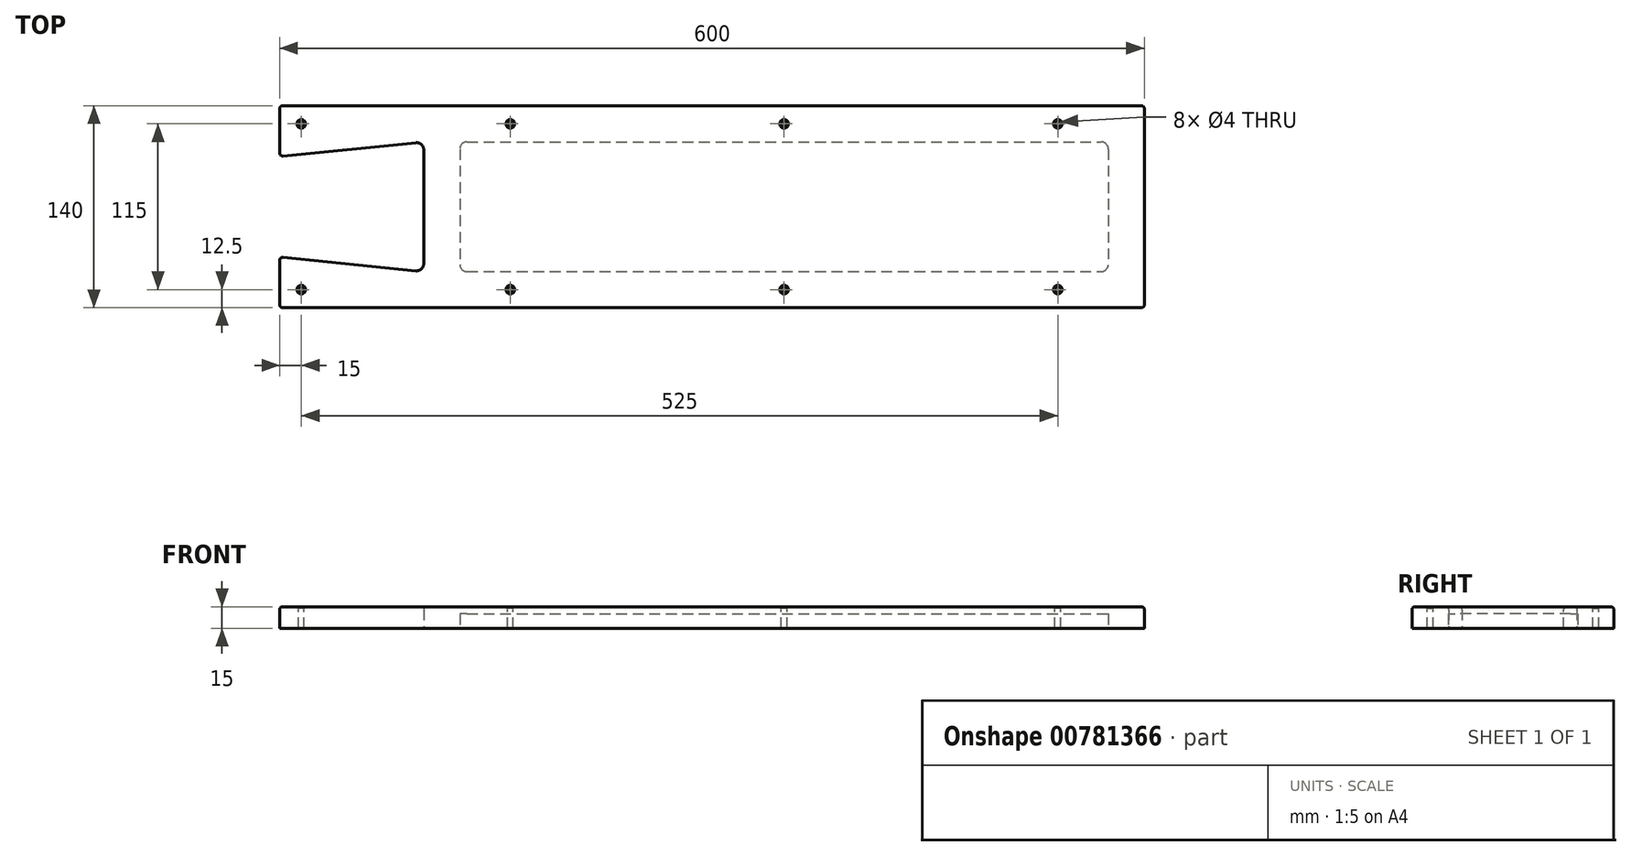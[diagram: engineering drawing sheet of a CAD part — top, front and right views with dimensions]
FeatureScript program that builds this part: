
annotation { "Feature Type Name" : "Feature", "Feature Type Description" : "" }
export const myFeature = defineFeature(function(context is Context, id is Id, definition is map)
    precondition{}
    {
        {
            var Q0;
            Q0=qCreatedBy(makeId("Top.planeOp"),FACE);
            var sketch = newSketch(context, id + "F0", { "sketchPlane" : qUnion([Q0])});
            skLineSegment(sketch, "E0.bottom", {"start": v(300, -70) * mm, "end": v(-300, -70) * mm});
            skLineSegment(sketch, "E0.top", {"start": v(300, 70) * mm, "end": v(-300, 70) * mm});
            skLineSegment(sketch, "E0.left", {"start": v(300, -70) * mm, "end": v(300, 70) * mm});
            skLineSegment(sketch, "E0.right", {"start": v(-300, -70) * mm, "end": v(-300, -35) * mm});
            skPoint(sketch, "E0.middle", {"position": v(0, 0) * mm});
            skLineSegment(sketch, "E1", {"start": v(0, 0) * mm, "end": v(-300, 0) * mm, "construction": true});
            skLineSegment(sketch, "E2", {"start": v(-300, 35) * mm, "end": v(-205.5, 44.45) * mm});
            skLineSegment(sketch, "E3", {"start": v(-200, 39.48) * mm, "end": v(-200, 0) * mm});
            skPoint(sketch, "E4.visualSharp", {"position": v(-200, 45) * mm});
            skArc(sketch, "E4.filletArc", {"start": v(-200, 39.48) * mm, "mid": v(-201.64, 43.18) * mm, "end": v(-205.5, 44.45) * mm});
            skLineSegment(sketch, "E5.MirrorCS", {"start": v(-300, -35) * mm, "end": v(-205.5, -44.45) * mm});
            skArc(sketch, "E6.MirrorCS", {"start": v(-200, -39.48) * mm, "mid": v(-201.64, -43.18) * mm, "end": v(-205.5, -44.45) * mm});
            skLineSegment(sketch, "E7.MirrorCS", {"start": v(-200, -39.48) * mm, "end": v(-200, 0) * mm});
            skLineSegment(sketch, "E8", {"start": v(-300, -35) * mm, "end": v(-300, 35) * mm, "construction": true});
            skLineSegment(sketch, "E9", {"start": v(-300, 35) * mm, "end": v(-300, 70) * mm});
            skSolve(sketch);
        }
        {
            var Q0;
            Q0=makeQuery(id+"F0.imprint","IMPRINT",FACE,{"disambiguationData":[TD([[makeQuery(id+"F0.imprint","IMPRINT",EDGE,{"derivedFrom":sQuery(id+"F0.wireOp",EDGE,"E0.bottom")}),-1.0]])]});
            extrude(context, id + "F1", {"entities" : qUnion([Q0]), "endBound" : BoundingType.SYMMETRIC, "depth" : 15 * mm, "offsetDistance" : 25 * mm});
        }
        {
            var Q0;
            Q0=makeQuery(id+"F1.opExtrude","CAP_FACE",FACE,{"disambiguationData":[OSD([sQuery(id+"F0.wireOp",EDGE,"E0.bottom"),sQuery(id+"F0.wireOp",EDGE,"E0.top"),sQuery(id+"F0.wireOp",EDGE,"E0.left"),sQuery(id+"F0.wireOp",EDGE,"E0.right"),sQuery(id+"F0.wireOp",EDGE,"E2"),sQuery(id+"F0.wireOp",EDGE,"E3"),sQuery(id+"F0.wireOp",EDGE,"E4.filletArc"),sQuery(id+"F0.wireOp",EDGE,"E5.MirrorCS"),sQuery(id+"F0.wireOp",EDGE,"E6.MirrorCS"),sQuery(id+"F0.wireOp",EDGE,"E7.MirrorCS"),sQuery(id+"F0.wireOp",EDGE,"E9")])],"isStart":true});
            var sketch = newSketch(context, id + "F2", { "sketchPlane" : qUnion([Q0])});
            skLineSegment(sketch, "E10", {"start": v(300, 0) * mm, "end": v(-200, 0) * mm, "construction": true});
            skLineSegment(sketch, "E11", {"start": v(-175, 0) * mm, "end": v(-175, 40) * mm});
            skLineSegment(sketch, "E12", {"start": v(-170, 45) * mm, "end": v(270, 45) * mm});
            skLineSegment(sketch, "E13", {"start": v(275, 40) * mm, "end": v(275, 0) * mm});
            skPoint(sketch, "E14.visualSharp", {"position": v(-175, 45) * mm});
            skArc(sketch, "E14.filletArc", {"start": v(-170, 45) * mm, "mid": v(-173.54, 43.54) * mm, "end": v(-175, 40) * mm});
            skPoint(sketch, "E15.visualSharp", {"position": v(275, 45) * mm});
            skArc(sketch, "E15.filletArc", {"start": v(275, 40) * mm, "mid": v(273.54, 43.54) * mm, "end": v(270, 45) * mm});
            skLineSegment(sketch, "E16.MirrorCS", {"start": v(-175, 0) * mm, "end": v(-175, -40) * mm});
            skArc(sketch, "E17.MirrorCS", {"start": v(-170, -45) * mm, "mid": v(-173.54, -43.54) * mm, "end": v(-175, -40) * mm});
            skLineSegment(sketch, "E18.MirrorCS", {"start": v(-170, -45) * mm, "end": v(270, -45) * mm});
            skArc(sketch, "E19.MirrorCS", {"start": v(275, -40) * mm, "mid": v(273.54, -43.54) * mm, "end": v(270, -45) * mm});
            skLineSegment(sketch, "E20.MirrorCS", {"start": v(275, -40) * mm, "end": v(275, 0) * mm});
            skSolve(sketch);
        }
        {
            var Q0;
            Q0=makeQuery(id+"F2.imprint","IMPRINT",FACE,{"disambiguationData":[TD([[makeQuery(id+"F2.imprint","IMPRINT",EDGE,{"derivedFrom":sQuery(id+"F2.wireOp",EDGE,"E11")}),-1.0]])]});
            extrude(context, id + "F3", {"entities" : qUnion([Q0]), "operationType" : NewBodyOperationType.REMOVE, "oppositeDirection" : true, "depth" : 10 * mm, "offsetDistance" : 25 * mm});
        }
        {
            var Q0;
            Q0=makeQuery(id+"F1.opExtrude","CAP_FACE",FACE,{"disambiguationData":[OSD([sQuery(id+"F0.wireOp",EDGE,"E0.bottom"),sQuery(id+"F0.wireOp",EDGE,"E0.top"),sQuery(id+"F0.wireOp",EDGE,"E0.left"),sQuery(id+"F0.wireOp",EDGE,"E0.right"),sQuery(id+"F0.wireOp",EDGE,"E2"),sQuery(id+"F0.wireOp",EDGE,"E3"),sQuery(id+"F0.wireOp",EDGE,"E4.filletArc"),sQuery(id+"F0.wireOp",EDGE,"E5.MirrorCS"),sQuery(id+"F0.wireOp",EDGE,"E6.MirrorCS"),sQuery(id+"F0.wireOp",EDGE,"E7.MirrorCS"),sQuery(id+"F0.wireOp",EDGE,"E9")])],"isStart":false});
            var sketch = newSketch(context, id + "F4", { "sketchPlane" : qUnion([Q0])});
            skLineSegment(sketch, "E21", {"start": v(-300, 57.5) * mm, "end": v(300, 57.5) * mm});
            skPoint(sketch, "E22", {"position": v(-285, 57.5) * mm});
            skLineSegment(sketch, "E23", {"start": v(0, 0) * mm, "end": v(-200, 0) * mm, "construction": true});
            skLineSegment(sketch, "E24.MirrorCS", {"start": v(-300, -57.5) * mm, "end": v(300, -57.5) * mm});
            skPoint(sketch, "E25.MirrorP", {"position": v(-285, -57.5) * mm});
            skPoint(sketch, "E26", {"position": v(-140, 57.5) * mm});
            skPoint(sketch, "E27", {"position": v(-140, -57.5) * mm});
            skPoint(sketch, "E28", {"position": v(50, 57.5) * mm});
            skPoint(sketch, "E29", {"position": v(50, -57.5) * mm});
            skPoint(sketch, "E30", {"position": v(240, 57.5) * mm});
            skPoint(sketch, "E31", {"position": v(240, -57.5) * mm});
            skSolve(sketch);
        }
        {
            var Q0;
            Q0=sQuery(id+"F4.wireOp",VERTEX,"E22");
            var Q1;
            Q1=sQuery(id+"F4.wireOp",VERTEX,"E25.MirrorP");
            var Q2;
            Q2=sQuery(id+"F4.wireOp",VERTEX,"E27");
            var Q3;
            Q3=sQuery(id+"F4.wireOp",VERTEX,"E29");
            var Q4;
            Q4=sQuery(id+"F4.wireOp",VERTEX,"b19b8d90-26c0-4fe6-9244-a1e454472f98");
            var Q5;
            Q5=sQuery(id+"F4.wireOp",VERTEX,"E31");
            var Q6;
            Q6=sQuery(id+"F4.wireOp",VERTEX,"E30");
            var Q7;
            Q7=sQuery(id+"F4.wireOp",VERTEX,"ee43db4b-3d80-4aee-841b-ccfbff939a96");
            var Q8;
            Q8=sQuery(id+"F4.wireOp",VERTEX,"E28");
            var Q9;
            Q9=sQuery(id+"F4.wireOp",VERTEX,"E26");
            var Q10;
            Q10=makeQuery(id+"F1.opExtrude","SWEPT_BODY",BODY,{"disambiguationData":[OSD([sQuery(id+"F0.wireOp",EDGE,"E0.bottom"),sQuery(id+"F0.wireOp",EDGE,"E0.top"),sQuery(id+"F0.wireOp",EDGE,"E0.left"),sQuery(id+"F0.wireOp",EDGE,"E0.right"),sQuery(id+"F0.wireOp",EDGE,"E2"),sQuery(id+"F0.wireOp",EDGE,"E3"),sQuery(id+"F0.wireOp",EDGE,"E4.filletArc"),sQuery(id+"F0.wireOp",EDGE,"E5.MirrorCS"),sQuery(id+"F0.wireOp",EDGE,"E6.MirrorCS"),sQuery(id+"F0.wireOp",EDGE,"E7.MirrorCS"),sQuery(id+"F0.wireOp",EDGE,"E9")])]});
            hole(context, id + "F5", {"style" : HoleStyle.C_SINK, "endStyle" : HoleEndStyle.THROUGH, "standardTappedOrClearance" : lookupTablePath({ "standard" : "ISO", "fit" : "Normal", "size" : "4", "type" : "Drilled" }), "standardBlindInLast" : lookupTablePath({ "fit" : "Standard", "standard" : "ISO", "size" : "4", "type" : "Drilled" }), "holeDiameter" : 4 * mm, "cSinkDiameter" : 6 * mm, "cSinkAngle" : 90 * degree, "majorDiameter" : 5 * mm, "isTappedThrough" : true, "tappedDepth" : 12 * mm, "tapClearance" : 3, "locations" : qUnion([Q0, Q1, Q2, Q3, Q4, Q5, Q6, Q7, Q8, Q9]), "scope" : qUnion([Q10])});
        }
        {
            var Q0;
            Q0=makeQuery(id+"F1.opExtrude","CAP_EDGE",EDGE,{"disambiguationData":[OSD([sQuery(id+"F0.wireOp",EDGE,"E0.bottom")])],"isStart":false});
            var Q1;
            Q1=makeQuery(id+"F1.opExtrude","CAP_EDGE",EDGE,{"disambiguationData":[OSD([sQuery(id+"F0.wireOp",EDGE,"E0.right")])],"isStart":false});
            var Q2;
            Q2=makeQuery(id+"F1.opExtrude","CAP_EDGE",EDGE,{"disambiguationData":[OSD([sQuery(id+"F0.wireOp",EDGE,"E5.MirrorCS")])],"isStart":false});
            var Q3;
            Q3=makeQuery(id+"F1.opExtrude","CAP_EDGE",EDGE,{"disambiguationData":[OSD([sQuery(id+"F0.wireOp",EDGE,"E0.top")])],"isStart":false});
            var Q4;
            Q4=makeQuery(id+"F1.opExtrude","CAP_EDGE",EDGE,{"disambiguationData":[OSD([sQuery(id+"F0.wireOp",EDGE,"E9")])],"isStart":false});
            var Q5;
            Q5=makeQuery(id+"F1.opExtrude","CAP_EDGE",EDGE,{"disambiguationData":[OSD([sQuery(id+"F0.wireOp",EDGE,"E0.left")])],"isStart":false});
            var Q6;
            Q6=makeQuery(id+"F3.boolean.opBoolean","COPY",EDGE,{"derivedFrom":makeQuery(id+"F3.opExtrude","CAP_EDGE",EDGE,{"disambiguationData":[OSD([sQuery(id+"F2.wireOp",EDGE,"E11"),sQuery(id+"F2.wireOp",EDGE,"E16.MirrorCS")])],"isStart":true})});
            var Q7;
            Q7=makeQuery(id+"F1.opExtrude","SWEPT_EDGE",EDGE,{"disambiguationData":[OSD([sQuery(id+"F0.wireOp",EDGE,"E2"),sQuery(id+"F0.wireOp",EDGE,"E9")])]});
            var Q8;
            Q8=makeQuery(id+"F1.opExtrude","SWEPT_EDGE",EDGE,{"disambiguationData":[OSD([sQuery(id+"F0.wireOp",EDGE,"E0.bottom"),sQuery(id+"F0.wireOp",EDGE,"E0.right")])]});
            var Q9;
            Q9=makeQuery(id+"F1.opExtrude","SWEPT_EDGE",EDGE,{"disambiguationData":[OSD([sQuery(id+"F0.wireOp",EDGE,"E0.top"),sQuery(id+"F0.wireOp",EDGE,"E9")])]});
            var Q10;
            Q10=makeQuery(id+"F1.opExtrude","SWEPT_EDGE",EDGE,{"disambiguationData":[OSD([sQuery(id+"F0.wireOp",EDGE,"E0.top"),sQuery(id+"F0.wireOp",EDGE,"E0.left")])]});
            var Q11;
            Q11=makeQuery(id+"F1.opExtrude","SWEPT_EDGE",EDGE,{"disambiguationData":[OSD([sQuery(id+"F0.wireOp",EDGE,"E0.bottom"),sQuery(id+"F0.wireOp",EDGE,"E0.left")])]});
            var Q12;
            Q12=makeQuery(id+"F1.opExtrude","SWEPT_EDGE",EDGE,{"disambiguationData":[OSD([sQuery(id+"F0.wireOp",EDGE,"E0.right"),sQuery(id+"F0.wireOp",EDGE,"E5.MirrorCS")])]});
            fillet(context, id + "F6", {"entities" : qUnion([Q0, Q1, Q2, Q3, Q4, Q5, Q6, Q7, Q8, Q9, Q10, Q11, Q12]), "radius" : 2 * mm, "tangentPropagation" : true, "allowEdgeOverflow" : false});
        }
    });
